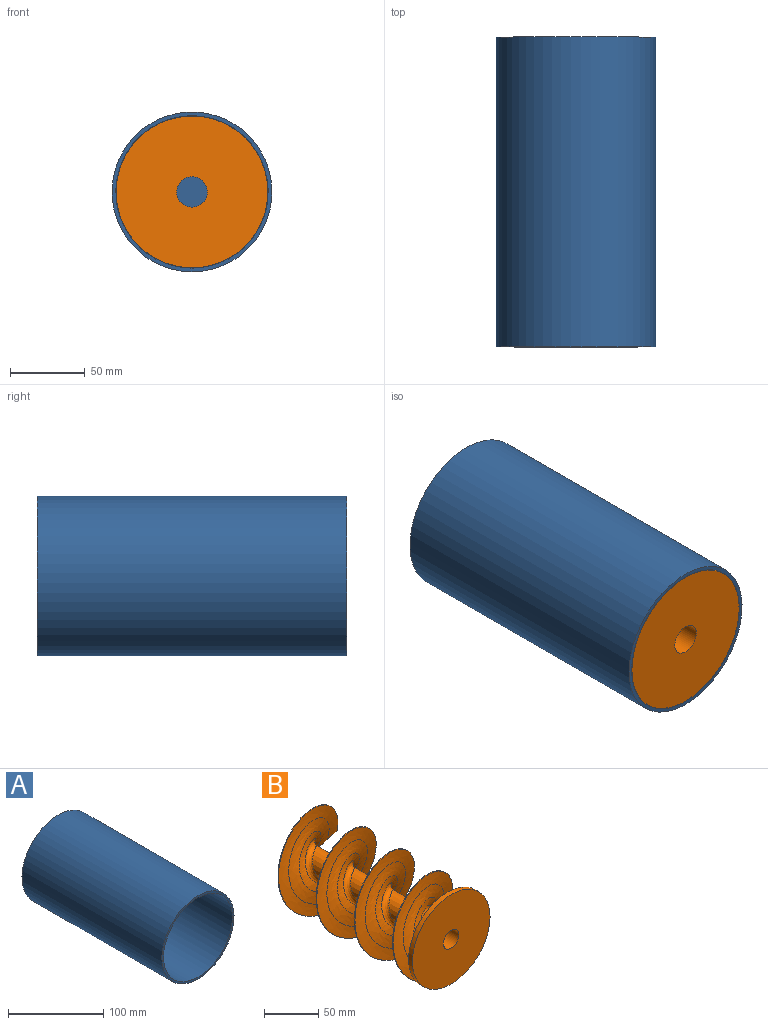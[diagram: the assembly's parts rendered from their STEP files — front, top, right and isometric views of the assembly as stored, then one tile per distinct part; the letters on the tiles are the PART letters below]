
ASSEMBLY  parts=2 mates=1
PART A: 8 faces, bbox 107x207.5x107 mm
  f0: cylinder r=51mm len=207.5mm, axis (0,-1,0), area 64301.3mm2, adj f2,f3,f4,f5,f6
  f1: cylinder r=53.5mm len=207.5mm, axis (0,-1,0), area 69751.2mm2, adj f3,f4
  f2: plane 102x102mm, normal (0,-1,0), area 7746.1mm2, adj f0,f5,f6,f7
  f3: plane 107x107mm, normal (0,-1,0), area 820.7mm2, adj f0,f1
  f4: plane 107x107mm, normal (0,1,0), area 8566.9mm2, adj f0,f1,f5,f6,f7
  f5: plane 18.07x7.5mm, normal (0.99,0,0.14), area 136.9mm2, adj f0,f2,f4,f7
  f6: plane 14.01x11.69mm, normal (-0.77,0,-0.64), area 136.9mm2, adj f0,f2,f4,f7
  f7: cylinder r=32.75mm len=16.44mm, axis (0,1,0), area 136.7mm2, adj f2,f4,f5,f6
PART B: 53 faces, bbox 105.1x207.6x105.1 mm
  f0: cylinder r=50.8mm len=101.6mm, axis (0,-1,0), area 1899.8mm2, adj f3,f14,f15,f23,f32,f33
  f1: extruded ~7.45x4.65mm, area 13.9mm2, adj f2,f38,f41,f42,f43
  f2: extruded ~14.22x1.38mm, area 17.1mm2, adj f1,f3,f35,f36,f39
  f3: extruded ~13.41x1mm, area 11.7mm2, adj f0,f2,f32,f33
  f4: extruded ~31.2x25.4mm, area 774.1mm2, adj f11,f37,f42,f45
  f5: bspline ~187.5x52.34mm, area 4209.2mm2, adj f6,f13,f43,f45,f46,f47,f48,f49
  f6: bspline ~187.5x78.4mm, area 9701.4mm2, adj f5,f7,f13,f39,f41
  f7: bspline ~187.5x102.82mm, area 13309.3mm2, adj f6,f13,f15,f33,f36
  f8: bspline ~195.83x102.82mm, area 14047.9mm2, adj f9,f13,f15,f23
  f9: bspline ~195.83x76.2mm, area 10205.2mm2, adj f8,f10,f13,f23
  f10: bspline ~195.83x52.02mm, area 4610.5mm2, adj f9,f13,f23,f24,f25,f26,f27,f28
  f11: cylinder r=12.7mm len=34.7mm, axis (0,1,0), area 183.7mm2, adj f4,f12,f34,f46
  f12: extruded ~81.2x25.39mm, area 2696.9mm2, adj f11,f18,f30,f31,f47
  f13: plane 65.75x27.66mm, normal (0,1,0), area 416.6mm2, adj f5,f6,f7,f8,f9,f10,f15,f21
  f14: plane 101.6x101.6mm, normal (0,-1,0), area 7780.5mm2, adj f0,f15,f21
  f15: bspline ~200x102.82mm, area 997.9mm2, adj f0,f7,f8,f13,f14
  f16: cylinder r=12.7mm len=39.86mm, axis (0,1,0), area 202.7mm2, adj f19,f22,f25,f52
  f17: cylinder r=12.7mm len=39.86mm, axis (0,1,0), area 202.7mm2, adj f19,f20,f27,f50
  f18: cylinder r=12.7mm len=39.86mm, axis (0,1,0), area 202.7mm2, adj f12,f20,f29,f48
  f19: extruded ~82.86x25.39mm, area 2698.4mm2, adj f16,f17,f26,f51
  f20: extruded ~82.86x25.39mm, area 2698.4mm2, adj f17,f18,f28,f49
  f21: cylinder r=10.2mm len=200mm, axis (0,1,0), area 12817.7mm2, adj f13,f14
  f22: extruded ~41.66x25.4mm, area 1363.3mm2, adj f13,f16,f24,f52
  f23: plane 101.8x96.39mm, normal (0,1,0), area 5325.4mm2, adj f0,f8,f9,f10,f31,f32,f34,f35
  f24: bspline ~50.88x34.23mm, area 641.8mm2, adj f10,f13,f22,f25
  f25: bspline ~9.66x8.4mm, area 50.9mm2, adj f10,f16,f24,f26
  f26: bspline ~52.17x34.23mm, area 678mm2, adj f10,f19,f25,f27
  f27: bspline ~9.66x8.4mm, area 50.9mm2, adj f10,f17,f26,f28
  f28: bspline ~52.17x34.23mm, area 678mm2, adj f10,f20,f27,f29
  f29: bspline ~9.66x8.4mm, area 50.9mm2, adj f10,f18,f28,f30
  f30: bspline ~51.62x34.24mm, area 657.2mm2, adj f10,f12,f29,f31
  f31: bspline ~6.47x6.28mm, area 28mm2, adj f10,f12,f23,f30,f34
  f32: bspline ~19.36x6.38mm, area 98.1mm2, adj f0,f3,f23,f35
  f33: bspline ~16.56x5.48mm, area 87.5mm2, adj f0,f3,f7,f36
  f34: torus R=17.7mm, axis (0,-1,0), area 50mm2, adj f11,f23,f31,f37
  f35: bspline ~24.4x7.73mm, area 117.4mm2, adj f2,f23,f32,f38
  f36: bspline ~6.21x5.05mm, area 16.1mm2, adj f2,f7,f33,f39
  f37: bspline ~41.29x35.41mm, area 421mm2, adj f4,f23,f34,f40
  f38: bspline ~14.16x11.18mm, area 74.1mm2, adj f1,f23,f35,f40
  f39: bspline ~15.27x5.37mm, area 80.8mm2, adj f2,f6,f36,f41
  f40: sphere r=5mm, area 27.5mm2, adj f37,f38,f42
  f41: bspline ~4.91x4.79mm, area 8.4mm2, adj f1,f6,f39,f43
  f42: cylinder r=5mm len=5.76mm, axis (0,1,0), area 11.1mm2, adj f1,f4,f40,f44
  f43: bspline ~8.95x8.15mm, area 46.9mm2, adj f1,f5,f41,f44
  f44: sphere r=5mm, area 18.8mm2, adj f42,f43,f45
  f45: bspline ~34.81x34.22mm, area 452.3mm2, adj f4,f5,f44,f46
  f46: bspline ~11.2x9.75mm, area 53.7mm2, adj f5,f11,f45,f47
  f47: bspline ~51.15x34.92mm, area 716.9mm2, adj f5,f12,f46,f48
  f48: bspline ~11.2x9.75mm, area 53.7mm2, adj f5,f18,f47,f49
  f49: bspline ~51.15x34.92mm, area 716.9mm2, adj f5,f20,f48,f50
  f50: bspline ~11.2x9.75mm, area 53.7mm2, adj f5,f17,f49,f51
  f51: bspline ~51.15x34.92mm, area 716.9mm2, adj f5,f19,f50,f52
  f52: bspline ~19.35x15.27mm, area 97.1mm2, adj f5,f13,f16,f22,f51
PLACE A t=(0.11,10.43,-7.5)mm
PLACE B t=(0.11,10.43,-7.5)mm
MATE revolute B.f21 <-> A.f1  axis (0,-1,0) through (0.11,-89.57,-7.5)mm
